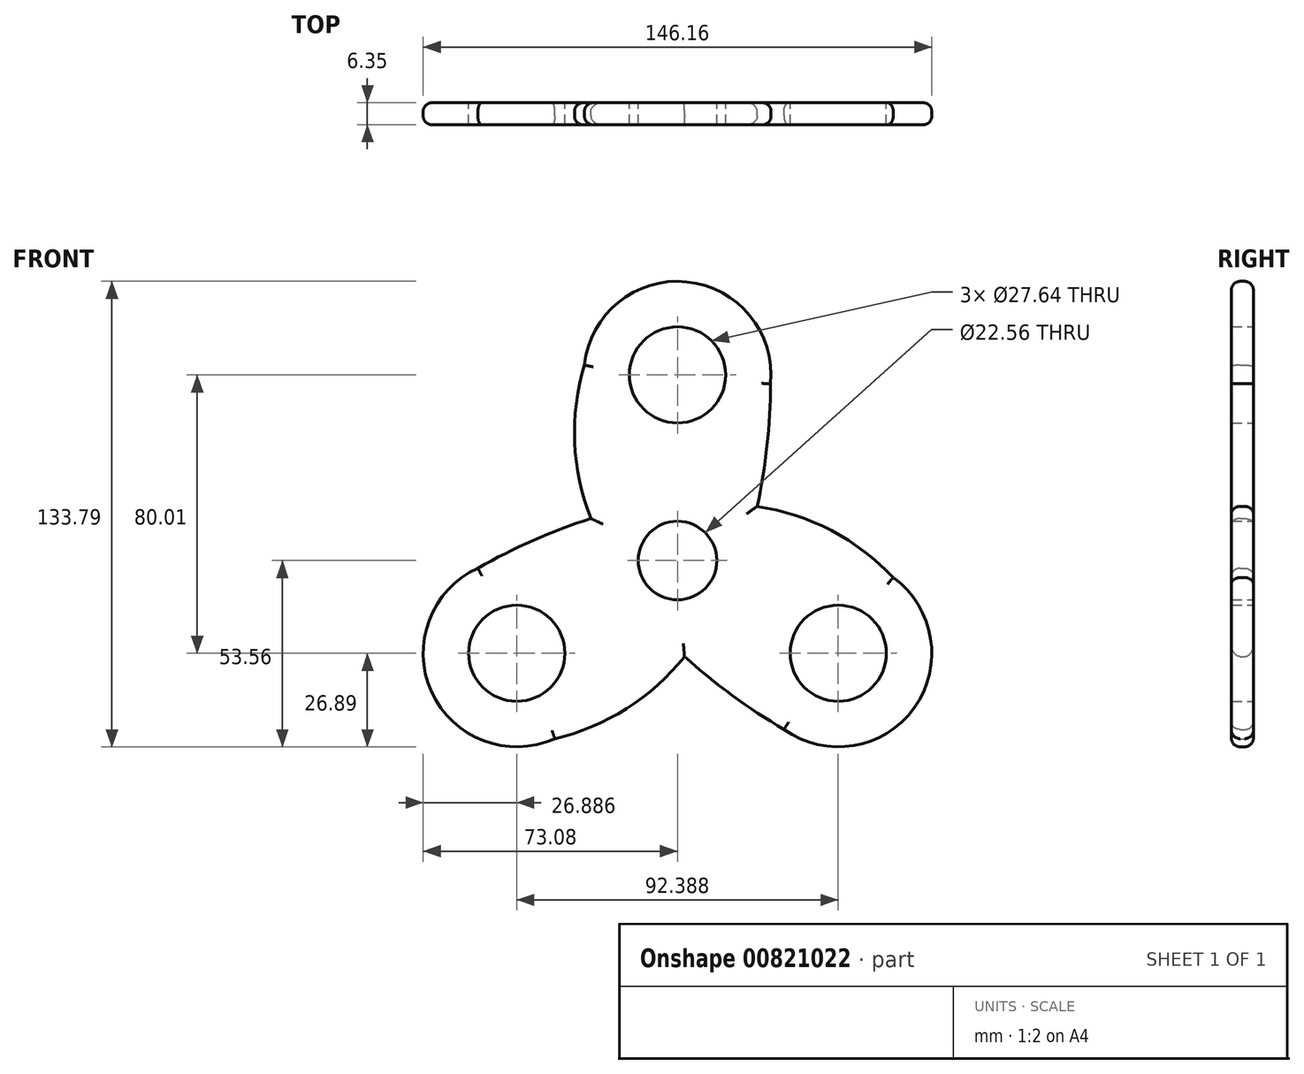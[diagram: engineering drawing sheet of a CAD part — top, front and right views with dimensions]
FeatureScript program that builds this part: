
annotation { "Feature Type Name" : "Feature", "Feature Type Description" : "" }
export const myFeature = defineFeature(function(context is Context, id is Id, definition is map)
    precondition{}
    {
        {
            var Q0;
            Q0=qCreatedBy(makeId("Front.planeOp"),FACE);
            var sketch = newSketch(context, id + "F0", { "sketchPlane" : qUnion([Q0])});
            skCircle(sketch, "E0", {"center": v(0, 0) * mm, "radius": 11.28 * mm});
            skCircle(sketch, "E1", {"center": v(0, 53.34) * mm, "radius": 13.82 * mm});
            skArc(sketch, "E2", {"start": v(26.77, 50.77) * mm, "mid": v(2.7, 80.1) * mm, "end": v(-26.74, 56.15) * mm});
            skArc(sketch, "E3", {"start": v(-26.74, 56.15) * mm, "mid": v(-29.56, 33.95) * mm, "end": v(-24.91, 12.07) * mm});
            skArc(sketch, "E4", {"start": v(22.9, 15.54) * mm, "mid": v(26.02, 35.86) * mm, "end": v(26.71, 56.42) * mm});
            skArc(sketch, "E5.1.0", {"start": v(-57.35, -2.2) * mm, "mid": v(-70.7, -37.72) * mm, "end": v(-35.26, -51.24) * mm});
            skArc(sketch, "E5.1.1", {"start": v(-35.26, -51.24) * mm, "mid": v(-14.63, -42.57) * mm, "end": v(2, -27.6) * mm});
            skArc(sketch, "E5.1.2", {"start": v(-24.91, 12.07) * mm, "mid": v(-44.07, 4.6) * mm, "end": v(-62.21, -5.07) * mm});
            skCircle(sketch, "E5.1.3", {"center": v(-46.2, -26.67) * mm, "radius": 13.82 * mm});
            skArc(sketch, "E5.2.0", {"start": v(30.59, -48.57) * mm, "mid": v(68.02, -42.38) * mm, "end": v(62, -4.92) * mm});
            skArc(sketch, "E5.2.1", {"start": v(62, -4.92) * mm, "mid": v(44.18, 8.62) * mm, "end": v(22.9, 15.54) * mm});
            skArc(sketch, "E5.2.2", {"start": v(2, -27.6) * mm, "mid": v(18.05, -40.47) * mm, "end": v(35.5, -51.34) * mm});
            skCircle(sketch, "E5.2.3", {"center": v(46.2, -26.67) * mm, "radius": 13.82 * mm});
            skPoint(sketch, "E6.orphan", {"position": v(-9.4, 16.28) * mm});
            skPoint(sketch, "E7.orphan", {"position": v(9.6, 16.17) * mm});
            skPoint(sketch, "E8.orphan", {"position": v(18.8, 0) * mm});
            skPoint(sketch, "E9.orphan", {"position": v(9.2, -16.4) * mm});
            skSolve(sketch);
        }
        {
            var Q0;
            Q0 = qSketchRegion(id + "F0", true);
            extrude(context, id + "F1", {"entities" : qUnion([Q0]), "depth" : 6.35 * mm, "offsetDistance" : 25.4 * mm});
        }
        {
            var Q0;
            Q0=makeQuery(id+"F1.opExtrude","CAP_EDGE",EDGE,{"disambiguationData":[OSD([sQuery(id+"F0.wireOp",EDGE,"E4")])],"isStart":false});
            var Q1;
            Q1=makeQuery(id+"F1.opExtrude","CAP_EDGE",EDGE,{"disambiguationData":[OSD([sQuery(id+"F0.wireOp",EDGE,"E2")])],"isStart":false});
            var Q2;
            Q2=makeQuery(id+"F1.opExtrude","CAP_EDGE",EDGE,{"disambiguationData":[OSD([sQuery(id+"F0.wireOp",EDGE,"E5.2.1")])],"isStart":false});
            var Q3;
            Q3=makeQuery(id+"F1.opExtrude","CAP_EDGE",EDGE,{"disambiguationData":[OSD([sQuery(id+"F0.wireOp",EDGE,"E5.2.0")])],"isStart":false});
            var Q4;
            Q4=makeQuery(id+"F1.opExtrude","CAP_EDGE",EDGE,{"disambiguationData":[OSD([sQuery(id+"F0.wireOp",EDGE,"E5.2.2")])],"isStart":false});
            var Q5;
            Q5=makeQuery(id+"F1.opExtrude","CAP_EDGE",EDGE,{"disambiguationData":[OSD([sQuery(id+"F0.wireOp",EDGE,"E5.1.1")])],"isStart":false});
            var Q6;
            Q6=makeQuery(id+"F1.opExtrude","CAP_EDGE",EDGE,{"disambiguationData":[OSD([sQuery(id+"F0.wireOp",EDGE,"E5.1.0")])],"isStart":false});
            var Q7;
            Q7=makeQuery(id+"F1.opExtrude","CAP_EDGE",EDGE,{"disambiguationData":[OSD([sQuery(id+"F0.wireOp",EDGE,"E5.1.2")])],"isStart":false});
            var Q8;
            Q8=makeQuery(id+"F1.opExtrude","CAP_EDGE",EDGE,{"disambiguationData":[OSD([sQuery(id+"F0.wireOp",EDGE,"E3")])],"isStart":false});
            fillet(context, id + "F2", {"entities" : qUnion([Q0, Q1, Q2, Q3, Q4, Q5, Q6, Q7, Q8]), "radius" : 2.54 * mm, "tangentPropagation" : true, "allowEdgeOverflow" : false});
        }
        {
            var Q0;
            Q0=makeQuery(id+"F1.opExtrude","CAP_EDGE",EDGE,{"disambiguationData":[OSD([sQuery(id+"F0.wireOp",EDGE,"E2")])],"isStart":true});
            var Q1;
            Q1=makeQuery(id+"F1.opExtrude","CAP_EDGE",EDGE,{"disambiguationData":[OSD([sQuery(id+"F0.wireOp",EDGE,"E3")])],"isStart":true});
            var Q2;
            Q2=makeQuery(id+"F1.opExtrude","CAP_EDGE",EDGE,{"disambiguationData":[OSD([sQuery(id+"F0.wireOp",EDGE,"E5.1.2")])],"isStart":true});
            var Q3;
            Q3=makeQuery(id+"F1.opExtrude","CAP_EDGE",EDGE,{"disambiguationData":[OSD([sQuery(id+"F0.wireOp",EDGE,"E5.1.0")])],"isStart":true});
            var Q4;
            Q4=makeQuery(id+"F1.opExtrude","CAP_EDGE",EDGE,{"disambiguationData":[OSD([sQuery(id+"F0.wireOp",EDGE,"E5.2.2")])],"isStart":true});
            var Q5;
            Q5=makeQuery(id+"F1.opExtrude","CAP_EDGE",EDGE,{"disambiguationData":[OSD([sQuery(id+"F0.wireOp",EDGE,"E5.2.0")])],"isStart":true});
            var Q6;
            Q6=makeQuery(id+"F1.opExtrude","CAP_EDGE",EDGE,{"disambiguationData":[OSD([sQuery(id+"F0.wireOp",EDGE,"E4")])],"isStart":true});
            var Q7;
            Q7=makeQuery(id+"F1.opExtrude","CAP_EDGE",EDGE,{"disambiguationData":[OSD([sQuery(id+"F0.wireOp",EDGE,"E5.1.1")])],"isStart":true});
            var Q8;
            Q8=makeQuery(id+"F1.opExtrude","CAP_EDGE",EDGE,{"disambiguationData":[OSD([sQuery(id+"F0.wireOp",EDGE,"E5.2.1")])],"isStart":true});
            fillet(context, id + "F3", {"entities" : qUnion([Q0, Q1, Q2, Q3, Q4, Q5, Q6, Q7, Q8]), "radius" : 2.54 * mm, "tangentPropagation" : true, "allowEdgeOverflow" : false});
        }
    });
